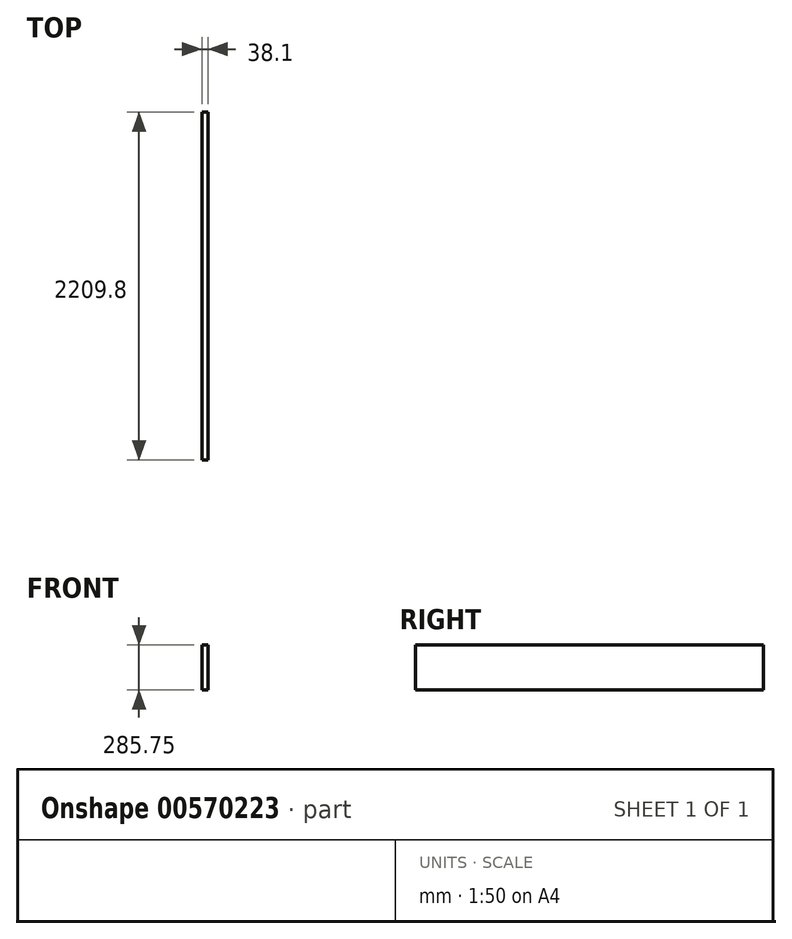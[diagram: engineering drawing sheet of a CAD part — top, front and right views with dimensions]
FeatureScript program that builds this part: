
annotation { "Feature Type Name" : "Feature", "Feature Type Description" : "" }
export const myFeature = defineFeature(function(context is Context, id is Id, definition is map)
    precondition{}
    {
        {
            var Q0;
            Q0=qCreatedBy(makeId("Front.planeOp"),FACE);
            var sketch = newSketch(context, id + "F0", { "sketchPlane" : qUnion([Q0])});
            skLineSegment(sketch, "E0.bottom", {"start": v(0, 0) * mm, "end": v(38.1, 0) * mm});
            skLineSegment(sketch, "E0.top", {"start": v(0, 285.75) * mm, "end": v(38.1, 285.75) * mm});
            skLineSegment(sketch, "E0.left", {"start": v(0, 0) * mm, "end": v(0, 285.75) * mm});
            skLineSegment(sketch, "E0.right", {"start": v(38.1, 0) * mm, "end": v(38.1, 285.75) * mm});
            skSolve(sketch);
        }
        {
            var Q0;
            Q0 = qSketchRegion(id + "F0", true);
            extrude(context, id + "F1", {"entities" : qUnion([Q0]), "depth" : 2209.8 * mm, "offsetDistance" : 25.4 * mm});
        }
    });
